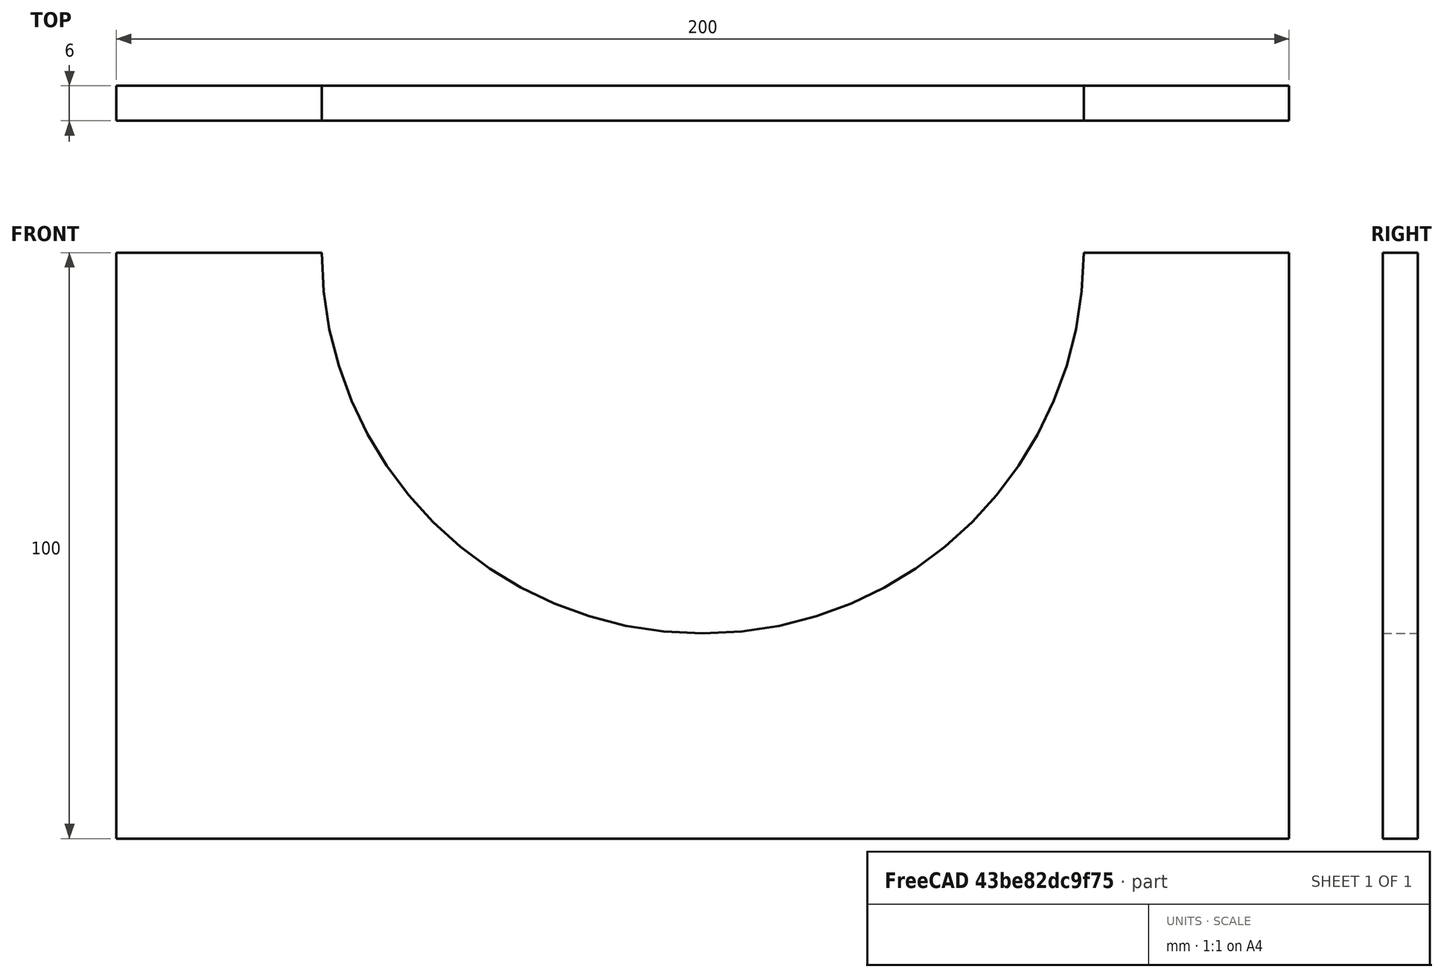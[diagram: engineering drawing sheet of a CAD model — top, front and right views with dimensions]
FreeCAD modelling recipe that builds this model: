
FCSTD DOCUMENT  (FreeCAD 0.18R4 (GitTag))
Label: soporte1
License: All rights reserved
LicenseURL: http://en.wikipedia.org/wiki/All_rights_reserved
objects: Sketcher::SketchObject×1, PartDesign::Pad×1, PartDesign::Body×1
note: 4 computed .brp shape members not serialized (recipe doc carries the construction recipe); baked Part::Feature solids carry a one-line shape summary decoded from their .brp

FEATURE [Sketcher::SketchObject] Sketch
  MapMode = 5
  Placement = pos=(0,0,0) rot=(1,0,0;1.5708rad)
  Support = -> [XZ_Plane]
  sketch-geometry (6):
    g0: LineSegment StartX=0 StartY=0 StartZ=0 EndX=200 EndY=0 EndZ=0
    g1: LineSegment StartX=200 StartY=0 StartZ=0 EndX=200 EndY=100 EndZ=0
    g2: LineSegment StartX=200 StartY=100 StartZ=0 EndX=165 EndY=100 EndZ=0
    g3: LineSegment StartX=0 StartY=100 StartZ=0 EndX=0 EndY=0 EndZ=0
    g4: ArcOfCircle CenterX=100 CenterY=100 CenterZ=0 NormalX=0 NormalY=0 NormalZ=1 AngleXU=0 Radius=65 StartAngle=3.14159 EndAngle=6.28319
    g5: LineSegment StartX=35 StartY=100 StartZ=0 EndX=0 EndY=100 EndZ=0
  constraints (17):
    c: Coincident(g0,g1)
    c: Coincident(g1,g2)
    c: Coincident(g3,g0)
    c: Horizontal(g0)
    c: Horizontal(g2)
    c: Vertical(g1)
    c: Vertical(g3)
    c: DistanceX(g0,g0) = 200
    c: DistanceY(g3,g3) = 100
    c: Coincident(g0,g-1)
    c: Radius(g4) = 65
    c: Coincident(g5,g4)
    c: Tangent(g2,g5)
    c: Coincident(g2,g4)
    c: Distance(g4,g3) = 100
    c: Distance(g4,g0) = 100
    c: Coincident(g3,g5)
FEATURE [PartDesign::Pad] Pad
  Length = 6
  Length2 = 100
  Placement = pos=(0,0,0) rot=(1,0,0;1.5708rad)
  Profile = -> Sketch
  Type = 0
FEATURE [PartDesign::Body] Body
  Group = -> [Sketch,Pad]
  Origin = -> Origin
  Tip = -> Pad
